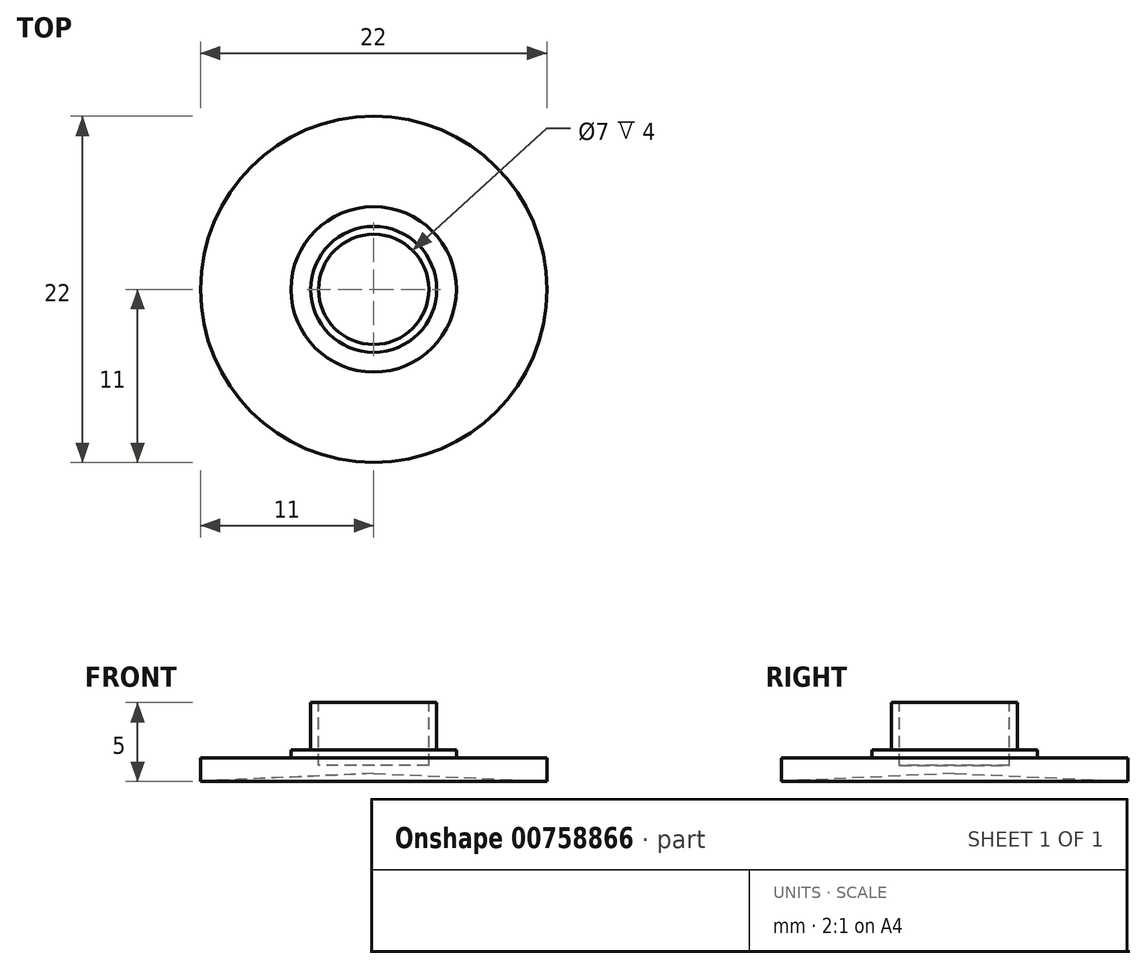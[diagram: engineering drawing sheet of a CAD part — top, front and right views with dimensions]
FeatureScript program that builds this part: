
annotation { "Feature Type Name" : "Feature", "Feature Type Description" : "" }
export const myFeature = defineFeature(function(context is Context, id is Id, definition is map)
    precondition{}
    {
        {
            var Q0;
            Q0=qCreatedBy(makeId("Front.planeOp"),FACE);
            var sketch = newSketch(context, id + "F0", { "sketchPlane" : qUnion([Q0])});
            skLineSegment(sketch, "E0", {"start": v(10.18, 0) * mm, "end": v(10.18, 1.5) * mm});
            skLineSegment(sketch, "E1", {"start": v(10.18, 1.5) * mm, "end": v(4.43, 1.5) * mm});
            skLineSegment(sketch, "E2", {"start": v(4.43, 1.5) * mm, "end": v(4.43, 2) * mm});
            skLineSegment(sketch, "E3", {"start": v(4.43, 2) * mm, "end": v(3.18, 2) * mm});
            skLineSegment(sketch, "E4", {"start": v(3.18, 2) * mm, "end": v(3.18, 5) * mm});
            skLineSegment(sketch, "E5", {"start": v(3.18, 5) * mm, "end": v(-0.82, 5) * mm});
            skLineSegment(sketch, "E6", {"start": v(-0.82, 5) * mm, "end": v(-0.82, 0.5) * mm});
            skPoint(sketch, "E7", {"position": v(-0.82, 0) * mm});
            skLineSegment(sketch, "E8", {"start": v(10.18, 0) * mm, "end": v(-0.82, 0.5) * mm});
            skSolve(sketch);
        }
        {
            var Q0;
            Q0=makeQuery(id+"F0.imprint","IMPRINT",FACE,{"disambiguationData":[TD([[makeQuery(id+"F0.imprint","IMPRINT",EDGE,{"derivedFrom":sQuery(id+"F0.wireOp",EDGE,"E0")}),1.0]])]});
            var Q1;
            Q1=sQuery(id+"F0.wireOp",EDGE,"E6");
            revolve(context, id + "F1", {"surfaceOperationType" : NewSurfaceOperationType.NEW, "entities" : qUnion([Q0]), "axis" : qUnion([Q1]), "revolveType" : RevolveType.FULL});
        }
        {
            var Q0;
            Q0=makeQuery(id+"F1.opRevolve","SWEPT_FACE",FACE,{"disambiguationData":[OSD([sQuery(id+"F0.wireOp",EDGE,"E5")])]});
            var sketch = newSketch(context, id + "F2", { "sketchPlane" : qUnion([Q0])});
            skCircle(sketch, "E9", {"center": v(-0.82, 0) * mm, "radius": 3.5 * mm});
            skSolve(sketch);
        }
        {
            var Q0;
            Q0=makeQuery(id+"F2.imprint","IMPRINT",FACE,{"disambiguationData":[TD([[makeQuery(id+"F2.imprint","IMPRINT",EDGE,{"derivedFrom":sQuery(id+"F2.wireOp",EDGE,"E9")}),1.0]])]});
            extrude(context, id + "F3", {"entities" : qUnion([Q0]), "operationType" : NewBodyOperationType.REMOVE, "oppositeDirection" : true, "depth" : 4 * mm, "offsetDistance" : 25 * mm});
        }
    });
